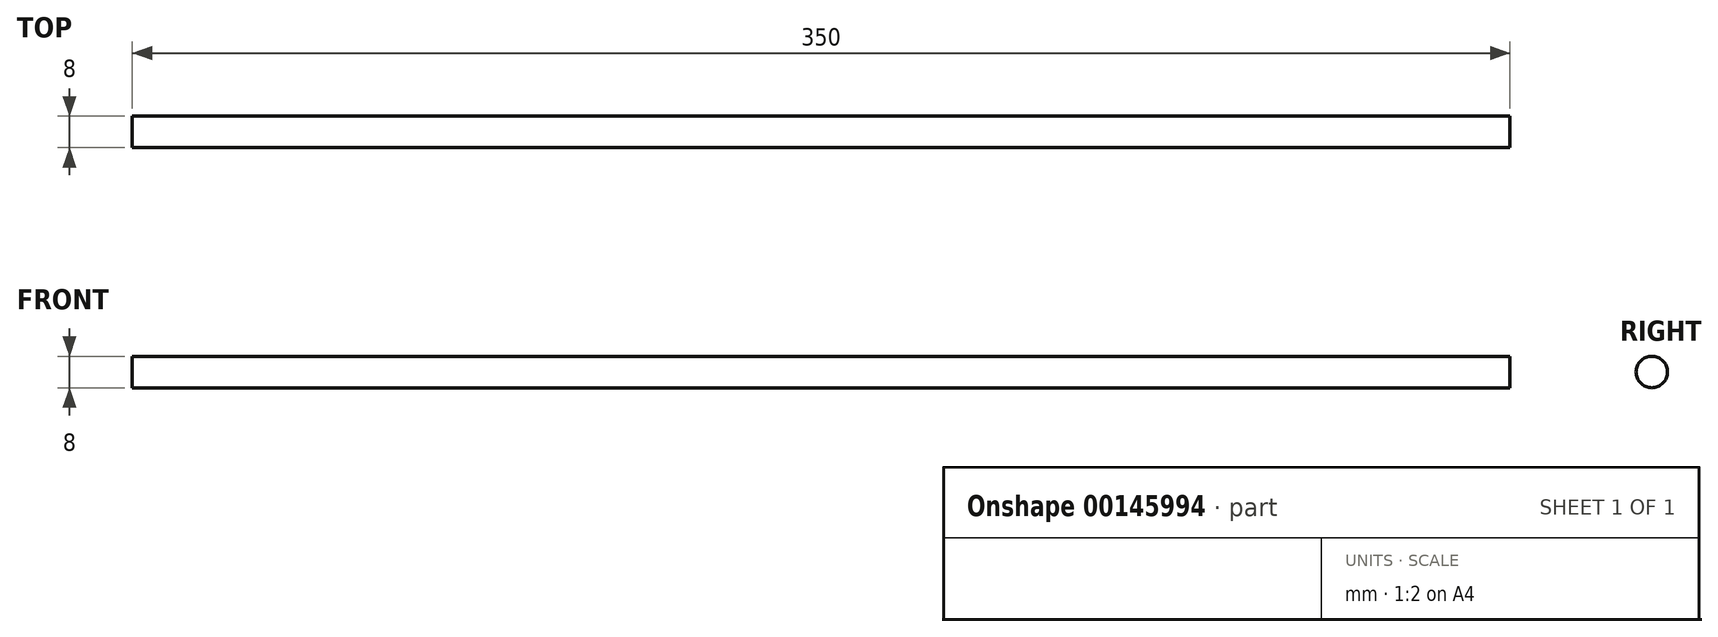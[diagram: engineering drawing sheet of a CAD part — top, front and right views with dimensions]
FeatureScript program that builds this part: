
annotation { "Feature Type Name" : "Feature", "Feature Type Description" : "" }
export const myFeature = defineFeature(function(context is Context, id is Id, definition is map)
    precondition{}
    {
        {
            var Q0;
            Q0=qCreatedBy(makeId("Right.planeOp"),FACE);
            var sketch = newSketch(context, id + "F0", { "sketchPlane" : qUnion([Q0])});
            skCircle(sketch, "E0", {"center": v(0, 0) * mm, "radius": 4 * mm});
            skSolve(sketch);
        }
        {
            var Q0;
            Q0 = qSketchRegion(id + "F0", true);
            extrude(context, id + "F1", {"entities" : qUnion([Q0]), "depth" : 350 * mm});
        }
    });
